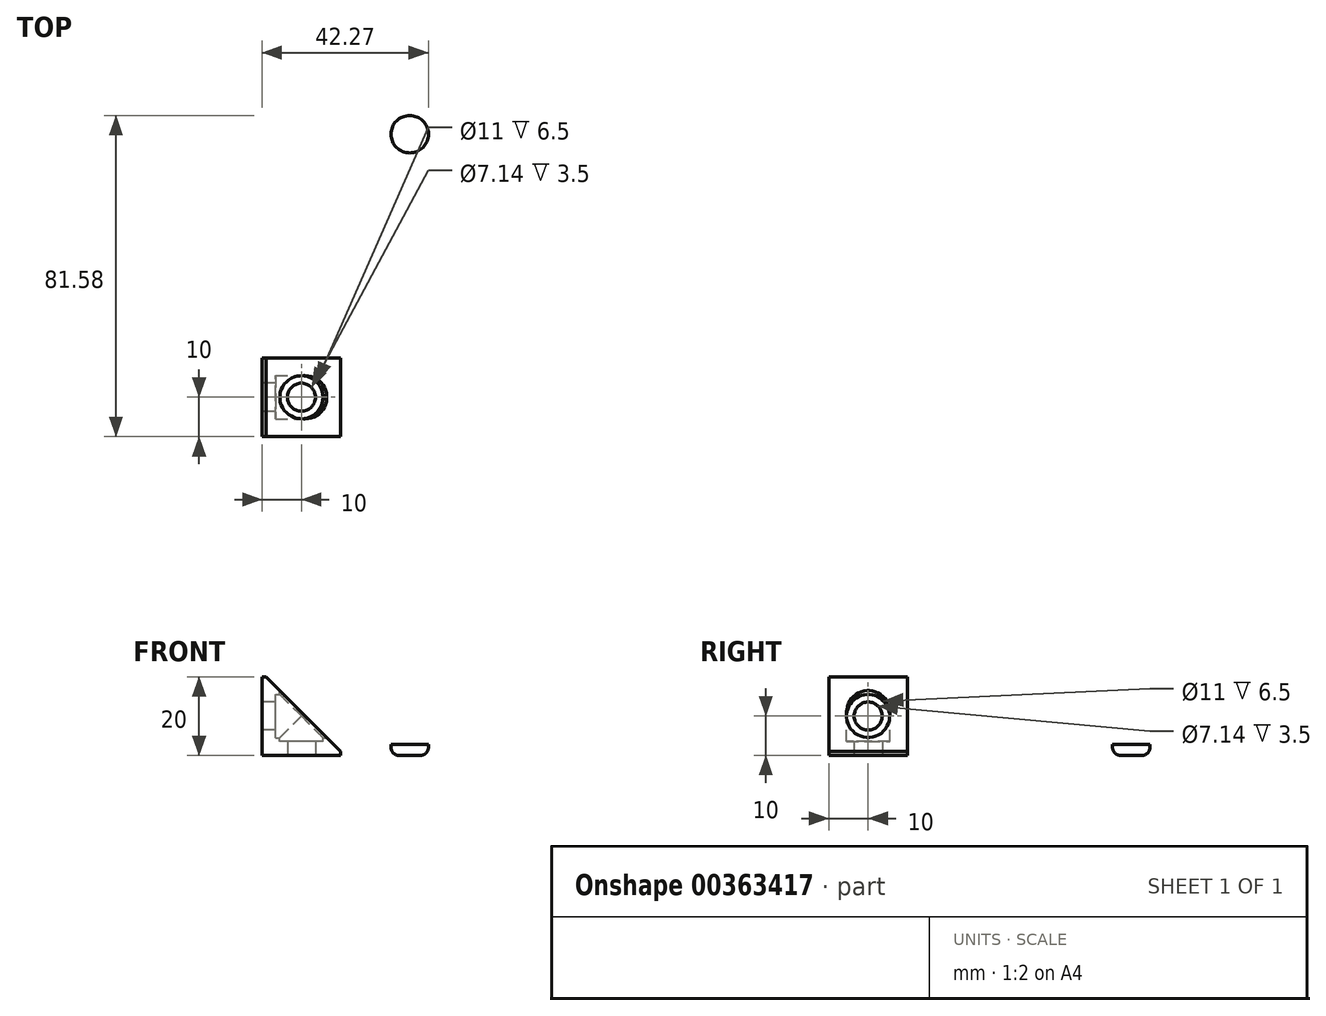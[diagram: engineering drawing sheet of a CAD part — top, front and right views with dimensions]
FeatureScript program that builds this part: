
annotation { "Feature Type Name" : "Feature", "Feature Type Description" : "" }
export const myFeature = defineFeature(function(context is Context, id is Id, definition is map)
    precondition{}
    {
        {
            var Q0;
            Q0=qCreatedBy(makeId("Front.planeOp"),FACE);
            var sketch = newSketch(context, id + "F0", { "sketchPlane" : qUnion([Q0])});
            skLineSegment(sketch, "E0", {"start": v(0, 0) * mm, "end": v(0, 20) * mm});
            skLineSegment(sketch, "E1", {"start": v(0, 20) * mm, "end": v(1, 20) * mm});
            skLineSegment(sketch, "E2", {"start": v(1, 20) * mm, "end": v(20, 1) * mm});
            skLineSegment(sketch, "E3", {"start": v(20, 1) * mm, "end": v(20, 0) * mm});
            skLineSegment(sketch, "E4", {"start": v(20, 0) * mm, "end": v(0, 0) * mm});
            skLineSegment(sketch, "E5", {"start": v(20, 1) * mm, "end": v(20, 20) * mm});
            skLineSegment(sketch, "E6", {"start": v(20, 20) * mm, "end": v(1, 20) * mm});
            skSolve(sketch);
        }
        {
            var Q0;
            Q0 = qSketchRegion(id + "F0", true);
            extrude(context, id + "F1", {"entities" : qUnion([Q0]), "depth" : 20 * mm, "offsetDistance" : 25 * mm});
        }
        {
            var Q0;
            Q0=makeQuery(id+"F1.opExtrude","SWEPT_FACE",FACE,{"disambiguationData":[OSD([sQuery(id+"F0.wireOp",EDGE,"E4")])]});
            var sketch = newSketch(context, id + "F2", { "sketchPlane" : qUnion([Q0])});
            skCircle(sketch, "E7", {"center": v(10, 10) * mm, "radius": 3.57 * mm});
            skPoint(sketch, "E7.centerSnap0", {"position": v(0, 10) * mm});
            skPoint(sketch, "E7.centerSnap1", {"position": v(10, 0) * mm});
            skSolve(sketch);
        }
        {
            var Q0;
            Q0=makeQuery(id+"F1.opExtrude","SWEPT_FACE",FACE,{"disambiguationData":[OSD([sQuery(id+"F0.wireOp",EDGE,"E0")])]});
            var sketch = newSketch(context, id + "F3", { "sketchPlane" : qUnion([Q0])});
            skCircle(sketch, "E8", {"center": v(10, 10) * mm, "radius": 3.57 * mm});
            skPoint(sketch, "E8.centerSnap0", {"position": v(20, 10) * mm});
            skPoint(sketch, "E8.centerSnap1", {"position": v(10, 0) * mm});
            skSolve(sketch);
        }
        {
            var Q0;
            Q0=makeQuery(id+"F1.opExtrude","SWEPT_FACE",FACE,{"disambiguationData":[OSD([sQuery(id+"F0.wireOp",EDGE,"E3"),sQuery(id+"F0.wireOp",EDGE,"E5")])]});
            var sketch = newSketch(context, id + "F4", { "sketchPlane" : qUnion([Q0])});
            skCircle(sketch, "E9", {"center": v(-10, 10) * mm, "radius": 5.5 * mm});
            skPoint(sketch, "E9.centerSnap0", {"position": v(-20, 10) * mm});
            skPoint(sketch, "E9.centerSnap1", {"position": v(-10, 0) * mm});
            skSolve(sketch);
        }
        {
            var Q0;
            Q0=makeQuery(id+"F1.opExtrude","SWEPT_FACE",FACE,{"disambiguationData":[OSD([sQuery(id+"F0.wireOp",EDGE,"E1"),sQuery(id+"F0.wireOp",EDGE,"E6")])]});
            var sketch = newSketch(context, id + "F5", { "sketchPlane" : qUnion([Q0])});
            skCircle(sketch, "E10", {"center": v(10, -10) * mm, "radius": 5.5 * mm});
            skPoint(sketch, "E10.centerSnap0", {"position": v(0, -10) * mm});
            skPoint(sketch, "E10.centerSnap1", {"position": v(10, 0) * mm});
            skSolve(sketch);
        }
        {
            var Q0;
            Q0=makeQuery(id+"F5.imprint","IMPRINT",FACE,{"disambiguationData":[TD([[makeQuery(id+"F5.imprint","IMPRINT",EDGE,{"derivedFrom":sQuery(id+"F5.wireOp",EDGE,"E10")}),1.0]])]});
            extrude(context, id + "F6", {"entities" : qUnion([Q0]), "operationType" : NewBodyOperationType.REMOVE, "oppositeDirection" : true, "depth" : 16.5 * mm, "offsetDistance" : 25 * mm});
        }
        {
            var Q0;
            Q0=makeQuery(id+"F4.imprint","IMPRINT",FACE,{"disambiguationData":[TD([[makeQuery(id+"F4.imprint","IMPRINT",EDGE,{"derivedFrom":sQuery(id+"F4.wireOp",EDGE,"E9")}),1.0]])]});
            extrude(context, id + "F7", {"entities" : qUnion([Q0]), "operationType" : NewBodyOperationType.REMOVE, "oppositeDirection" : true, "depth" : 16.5 * mm, "offsetDistance" : 25 * mm});
        }
        {
            var Q0;
            Q0=makeQuery(id+"F3.imprint","IMPRINT",FACE,{"disambiguationData":[TD([[makeQuery(id+"F3.imprint","IMPRINT",EDGE,{"derivedFrom":sQuery(id+"F3.wireOp",EDGE,"E8")}),1.0]])]});
            extrude(context, id + "F8", {"entities" : qUnion([Q0]), "operationType" : NewBodyOperationType.REMOVE, "endBound" : BoundingType.THROUGH_ALL, "oppositeDirection" : true, "depth" : 25 * mm, "offsetDistance" : 25 * mm});
        }
        {
            var Q0;
            Q0=makeQuery(id+"F2.imprint","IMPRINT",FACE,{"disambiguationData":[TD([[makeQuery(id+"F2.imprint","IMPRINT",EDGE,{"derivedFrom":sQuery(id+"F2.wireOp",EDGE,"E7")}),1.0]])]});
            extrude(context, id + "F9", {"entities" : qUnion([Q0]), "operationType" : NewBodyOperationType.REMOVE, "endBound" : BoundingType.THROUGH_ALL, "oppositeDirection" : true, "depth" : 25 * mm, "offsetDistance" : 25 * mm});
        }
        {
            var Q0;
            Q0=makeQuery(id+"F0.imprint","IMPRINT",FACE,{"disambiguationData":[TD([[makeQuery(id+"F0.imprint","IMPRINT",EDGE,{"derivedFrom":sQuery(id+"F0.wireOp",EDGE,"E2")}),1.0]])]});
            extrude(context, id + "F10", {"entities" : qUnion([Q0]), "operationType" : NewBodyOperationType.REMOVE, "endBound" : BoundingType.THROUGH_ALL, "depth" : 25 * mm, "offsetDistance" : 25 * mm});
        }
        {
            var Q0;
            Q0=qCreatedBy(makeId("Top.planeOp"),FACE);
            var sketch = newSketch(context, id + "F11", { "sketchPlane" : qUnion([Q0])});
            skCircle(sketch, "E11", {"center": v(37.52, 56.83) * mm, "radius": 4.75 * mm});
            skSolve(sketch);
        }
        {
            var Q0;
            Q0=makeQuery(id+"F11.imprint","IMPRINT",FACE,{"disambiguationData":[TD([[makeQuery(id+"F11.imprint","IMPRINT",EDGE,{"derivedFrom":sQuery(id+"F11.wireOp",EDGE,"E11")}),1.0]])]});
            extrude(context, id + "F12", {"entities" : qUnion([Q0]), "depth" : 2.75 * mm, "offsetDistance" : 25 * mm});
        }
        {
            var Q0;
            Q0=makeQuery(id+"F12.opExtrude","CAP_EDGE",EDGE,{"disambiguationData":[OSD([sQuery(id+"F11.wireOp",EDGE,"E11")])],"isStart":true});
            fillet(context, id + "F13", {"entities" : qUnion([Q0]), "radius" : 2 * mm, "tangentPropagation" : true, "allowEdgeOverflow" : false});
        }
    });
